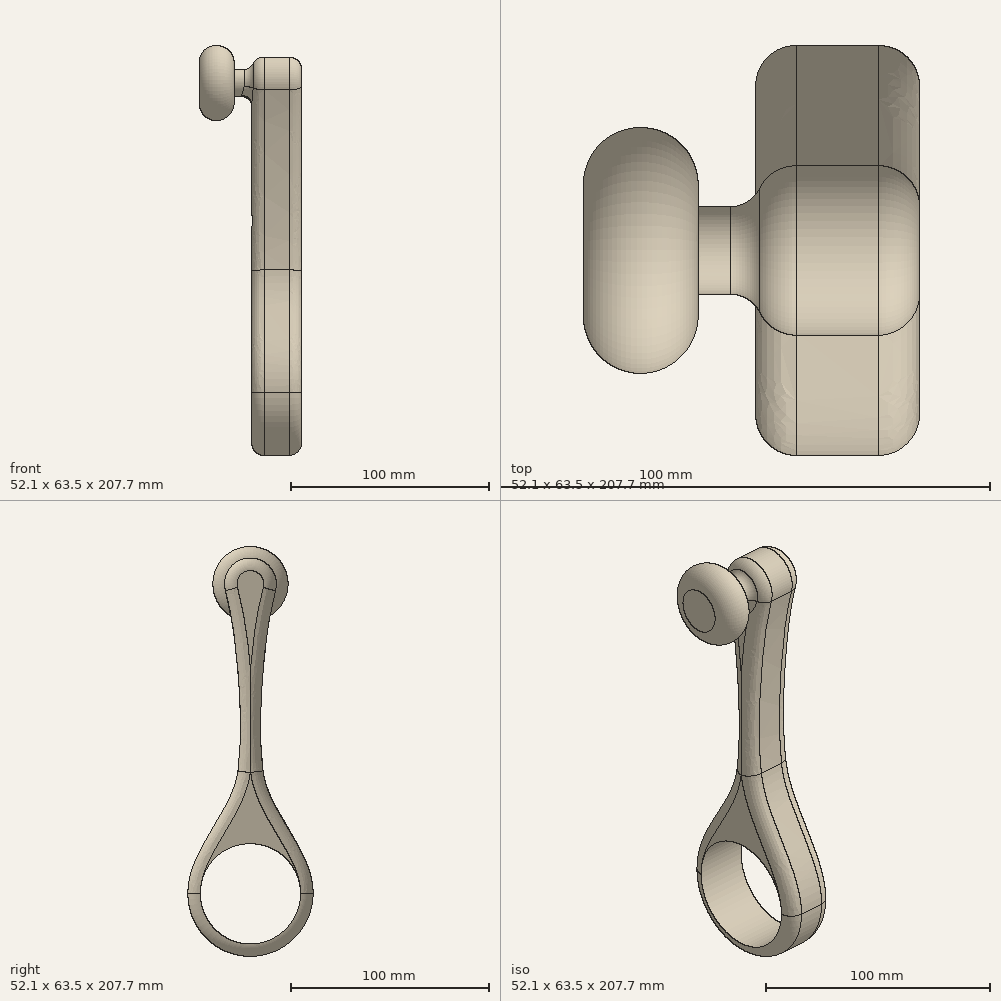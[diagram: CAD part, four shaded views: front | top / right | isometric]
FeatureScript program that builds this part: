
annotation { "Feature Type Name" : "Feature", "Feature Type Description" : "" }
export const myFeature = defineFeature(function(context is Context, id is Id, definition is map)
    precondition{}
    {
        {
            var Q0;
            Q0=qCreatedBy(makeId("Right.planeOp"),FACE);
            var sketch = newSketch(context, id + "F0", { "sketchPlane" : qUnion([Q0])});
            skCircle(sketch, "E0", {"center": v(0, 0) * mm, "radius": 25.4 * mm});
            skCircle(sketch, "E1.0", {"center": v(0, 0) * mm, "radius": 31.75 * mm});
            skLineSegment(sketch, "E2.bottom", {"start": v(-6.35, 24.6) * mm, "end": v(6.35, 24.6) * mm, "construction": true});
            skLineSegment(sketch, "E3", {"start": v(-12.7, 29.1) * mm, "end": v(12.7, 29.1) * mm, "construction": true});
            skPoint(sketch, "E4", {"position": v(-6.35, 62.27) * mm});
            skPoint(sketch, "E5", {"position": v(-6.35, 113.48) * mm});
            skPoint(sketch, "E6", {"position": v(0, 88.1) * mm});
            skPoint(sketch, "E6.positionSnap0", {"position": v(-6.35, 88.1) * mm});
            skFitSpline(sketch, "E7", {"points": [v(-12.7, 153.55) * mm, v(-6.35, 113.48) * mm, v(-6.35, 62.27) * mm, v(-12.7, 29.1) * mm], "startDerivative": vector(29.09, -109.51) * mm, "endDerivative": vector(-12.09, -104.65) * mm});
            skFitSpline(sketch, "E8", {"points": [v(-6.35, 62.27) * mm, v(-31.75, 0) * mm], "startDerivative": vector(-9.02, -67.04) * mm, "endDerivative": vector(0, -67.64) * mm});
            skFitSpline(sketch, "E9.MirrorCS", {"points": [v(6.35, 62.27) * mm, v(31.75, 0) * mm], "startDerivative": vector(9.02, -67.04) * mm, "endDerivative": vector(0, -67.64) * mm});
            skFitSpline(sketch, "E10.MirrorCS", {"points": [v(12.7, 153.55) * mm, v(6.35, 113.48) * mm, v(6.35, 62.27) * mm, v(12.7, 29.1) * mm], "startDerivative": vector(-29.09, -109.51) * mm, "endDerivative": vector(12.09, -104.65) * mm});
            skArc(sketch, "E11", {"start": v(12.7, 153.55) * mm, "mid": v(0, 170.06) * mm, "end": v(-12.7, 153.55) * mm});
            skFitSpline(sketch, "E12", {"points": [v(12.7, 153.55) * mm, v(6.35, 113.48) * mm, v(6.35, 62.27) * mm, v(12.7, 29.1) * mm], "startDerivative": vector(-29.09, -109.51) * mm, "endDerivative": vector(12.09, -104.65) * mm, "construction": true});
            skFitSpline(sketch, "E13", {"points": [v(-12.7, 153.55) * mm, v(-6.35, 113.48) * mm, v(-6.35, 62.27) * mm, v(-12.7, 29.1) * mm], "startDerivative": vector(29.09, -109.51) * mm, "endDerivative": vector(-12.09, -104.65) * mm, "construction": true});
            skSolve(sketch);
        }
        {
            var Q0;
            {var subQ5=sQuery(id+"F0.wireOp",EDGE,"E11");Q0=makeQuery(id+"F0.imprint","IMPRINT",FACE,{"disambiguationData":[TD([[makeQuery(id+"F0.imprint","IMPRINT",EDGE,{"derivedFrom":subQ5}),1.0]])]});}
            var Q1;
            {var subQ0=sQuery(id+"F0.wireOp",EDGE,"E7");var subQ1=sQuery(id+"F0.wireOp",EDGE,"E1.0");var subQ2=makeQuery(id+"F0.imprint","INTERSECT",VERTEX,{"derivedFrom":[subQ1,subQ0]});Q1=makeQuery(id+"F0.imprint","IMPRINT",FACE,{"disambiguationData":[TD([[makeQuery(id+"F0.imprint","IMPRINT",EDGE,{"disambiguationData":[TD([[subQ2,-1.0]])],"derivedFrom":subQ1}),-1.0]])]});}
            var Q2;
            {var subQ0=sQuery(id+"F0.wireOp",EDGE,"E9.MirrorCS");Q2=makeQuery(id+"F0.imprint","IMPRINT",FACE,{"disambiguationData":[TD([[makeQuery(id+"F0.imprint","IMPRINT",EDGE,{"derivedFrom":subQ0}),-1.0]])]});}
            var Q3;
            Q3=makeQuery(id+"F0.imprint","IMPRINT",FACE,{"disambiguationData":[TD([[makeQuery(id+"F0.imprint","IMPRINT",EDGE,{"derivedFrom":sQuery(id+"F0.wireOp",EDGE,"E0")}),-1.0]])]});
            extrude(context, id + "F1", {"entities" : qUnion([Q0, Q1, Q2, Q3]), "depth" : 25.4 * mm, "offsetDistance" : 25.4 * mm});
        }
        {
            var Q0;
            Q0=makeQuery(id+"F1.opExtrude","CAP_EDGE",EDGE,{"disambiguationData":[OSD([sQuery(id+"F0.wireOp",EDGE,"E9.MirrorCS")])],"isStart":true});
            var Q1;
            Q1=makeQuery(id+"F1.opExtrude","CAP_EDGE",EDGE,{"disambiguationData":[OSD([sQuery(id+"F0.wireOp",EDGE,"E7")])],"isStart":false});
            fillet(context, id + "F2", {"entities" : qUnion([Q0, Q1]), "radius" : 6.35 * mm, "tangentPropagation" : true, "allowEdgeOverflow" : false});
        }
        {
            var Q0;
            Q0=makeQuery(id+"F2.opFillet","SPLIT",FACE,{"disambiguationData":[OD(1.0)],"derivedFrom":makeQuery(id+"F1.opExtrude","CAP_FACE",FACE,{"disambiguationData":[OSD([sQuery(id+"F0.wireOp",EDGE,"E0"),sQuery(id+"F0.wireOp",EDGE,"E1.0"),sQuery(id+"F0.wireOp",EDGE,"E7"),sQuery(id+"F0.wireOp",EDGE,"E8"),sQuery(id+"F0.wireOp",EDGE,"E9.MirrorCS"),sQuery(id+"F0.wireOp",EDGE,"E10.MirrorCS"),sQuery(id+"F0.wireOp",EDGE,"E11")])],"isStart":true})});
            var sketch = newSketch(context, id + "F3", { "sketchPlane" : qUnion([Q0])});
            skCircle(sketch, "E14", {"center": v(0, 156.92) * mm, "radius": 6.8 * mm});
            skSolve(sketch);
        }
        {
            var Q0;
            {var subQ0=sQuery(id+"F3.wireOp",EDGE,"E14");var subQ1=sQuery(id+"F0.wireOp",EDGE,"E10.MirrorCS");var subQ2=sQuery(id+"F0.wireOp",EDGE,"E7");var subQ3=makeQuery(id+"F1.opExtrude","CAP_FACE",FACE,{"disambiguationData":[OSD([sQuery(id+"F0.wireOp",EDGE,"E0"),sQuery(id+"F0.wireOp",EDGE,"E1.0"),subQ2,sQuery(id+"F0.wireOp",EDGE,"E8"),sQuery(id+"F0.wireOp",EDGE,"E9.MirrorCS"),subQ1,sQuery(id+"F0.wireOp",EDGE,"E11")])],"isStart":true});var subQ4=makeQuery(id+"F3.imprint","INTERSECT",VERTEX,{"derivedFrom":[makeQuery(id+"F2.opFillet","BLEND_EDGE",EDGE,{"disambiguationData":[OD(1.0)],"blendedFrom":[makeQuery(id+"F1.opExtrude","CAP_EDGE",EDGE,{"disambiguationData":[OSD([subQ2])],"isStart":true}),subQ3],"blendedInto":[subQ3]}),subQ0]});Q0=makeQuery(id+"F3.imprint","IMPRINT",FACE,{"disambiguationData":[TD([[makeQuery(id+"F3.imprint","IMPRINT",EDGE,{"disambiguationData":[TD([[subQ4,1.0]])],"derivedFrom":subQ0}),1.0]])]});}
            extrude(context, id + "F4", {"entities" : qUnion([Q0]), "operationType" : NewBodyOperationType.ADD, "depth" : 17.78 * mm, "offsetDistance" : 25.4 * mm});
        }
        {
            var Q0;
            {var subQ0=sQuery(id+"F0.wireOp",EDGE,"E11");Q0=makeQuery(id+"F4.boolean.opBoolean","MERGE",EDGE,{"derivedFrom":[makeQuery(id+"F2.opFillet","BLEND_EDGE",EDGE,{"blendedFrom":[makeQuery(id+"F1.opExtrude","CAP_EDGE",EDGE,{"disambiguationData":[OSD([subQ0])],"isStart":true}),makeQuery(id+"F1.opExtrude","CAP_FACE",FACE,{"disambiguationData":[OSD([sQuery(id+"F0.wireOp",EDGE,"E0"),sQuery(id+"F0.wireOp",EDGE,"E1.0"),sQuery(id+"F0.wireOp",EDGE,"E7"),sQuery(id+"F0.wireOp",EDGE,"E8"),sQuery(id+"F0.wireOp",EDGE,"E9.MirrorCS"),sQuery(id+"F0.wireOp",EDGE,"E10.MirrorCS"),subQ0])],"isStart":true})],"blendedInto":[makeQuery(id+"F1.opExtrude","CAP_FACE",FACE,{"disambiguationData":[OSD([sQuery(id+"F0.wireOp",EDGE,"E0"),sQuery(id+"F0.wireOp",EDGE,"E1.0"),sQuery(id+"F0.wireOp",EDGE,"E7"),sQuery(id+"F0.wireOp",EDGE,"E8"),sQuery(id+"F0.wireOp",EDGE,"E9.MirrorCS"),sQuery(id+"F0.wireOp",EDGE,"E10.MirrorCS"),subQ0])],"isStart":true})]}),makeQuery(id+"F4.opExtrude","CAP_EDGE",EDGE,{"disambiguationData":[OSD([sQuery(id+"F3.wireOp",EDGE,"E14")])],"isStart":true})]});}
            var Q1;
            Q1=makeQuery(id+"F4.boolean.opBoolean","SPLIT",EDGE,{"derivedFrom":makeQuery(id+"F4.opExtrude","CAP_EDGE",EDGE,{"disambiguationData":[OSD([sQuery(id+"F3.wireOp",EDGE,"E14")])],"isStart":true})});
            fillet(context, id + "F5", {"entities" : qUnion([Q0, Q1]), "radius" : 5.08 * mm, "tangentPropagation" : true, "allowEdgeOverflow" : false});
        }
        {
            var Q0;
            Q0=makeQuery(id+"F4.opExtrude","CAP_FACE",FACE,{"disambiguationData":[OSD([sQuery(id+"F3.wireOp",EDGE,"E14")])],"isStart":false});
            var sketch = newSketch(context, id + "F6", { "sketchPlane" : qUnion([Q0])});
            skCircle(sketch, "E15", {"center": v(0, 156.92) * mm, "radius": 19.05 * mm});
            skSolve(sketch);
        }
        {
            var Q0;
            Q0=makeQuery(id+"F6.imprint","IMPRINT",FACE,{"disambiguationData":[TD([[makeQuery(id+"F6.imprint","IMPRINT",EDGE,{"derivedFrom":sQuery(id+"F6.wireOp",EDGE,"E15")}),1.0]])]});
            var Q1;
            Q1=makeQuery(id+"F6.imprint","IMPRINT",FACE,{"disambiguationData":[TD([[makeQuery(id+"F6.imprint","IMPRINT",EDGE,{"derivedFrom":makeQuery(id+"F4.opExtrude","CAP_EDGE",EDGE,{"disambiguationData":[OSD([sQuery(id+"F3.wireOp",EDGE,"E14")])],"isStart":false})}),1.0]])]});
            extrude(context, id + "F7", {"entities" : qUnion([Q0, Q1]), "depth" : 17.78 * mm, "offsetDistance" : 25.4 * mm, "symmetric" : true});
        }
        {
            var Q0;
            Q0=makeQuery(id+"F7.opExtrude","CAP_EDGE",EDGE,{"disambiguationData":[OSD([sQuery(id+"F6.wireOp",EDGE,"E15")])],"isStart":false});
            var Q1;
            Q1=makeQuery(id+"F7.opExtrude","CAP_EDGE",EDGE,{"disambiguationData":[OSD([sQuery(id+"F6.wireOp",EDGE,"E15")])],"isStart":true});
            fillet(context, id + "F8", {"entities" : qUnion([Q0, Q1]), "radius" : 8.9 * mm, "tangentPropagation" : true, "allowEdgeOverflow" : false});
        }
    });
